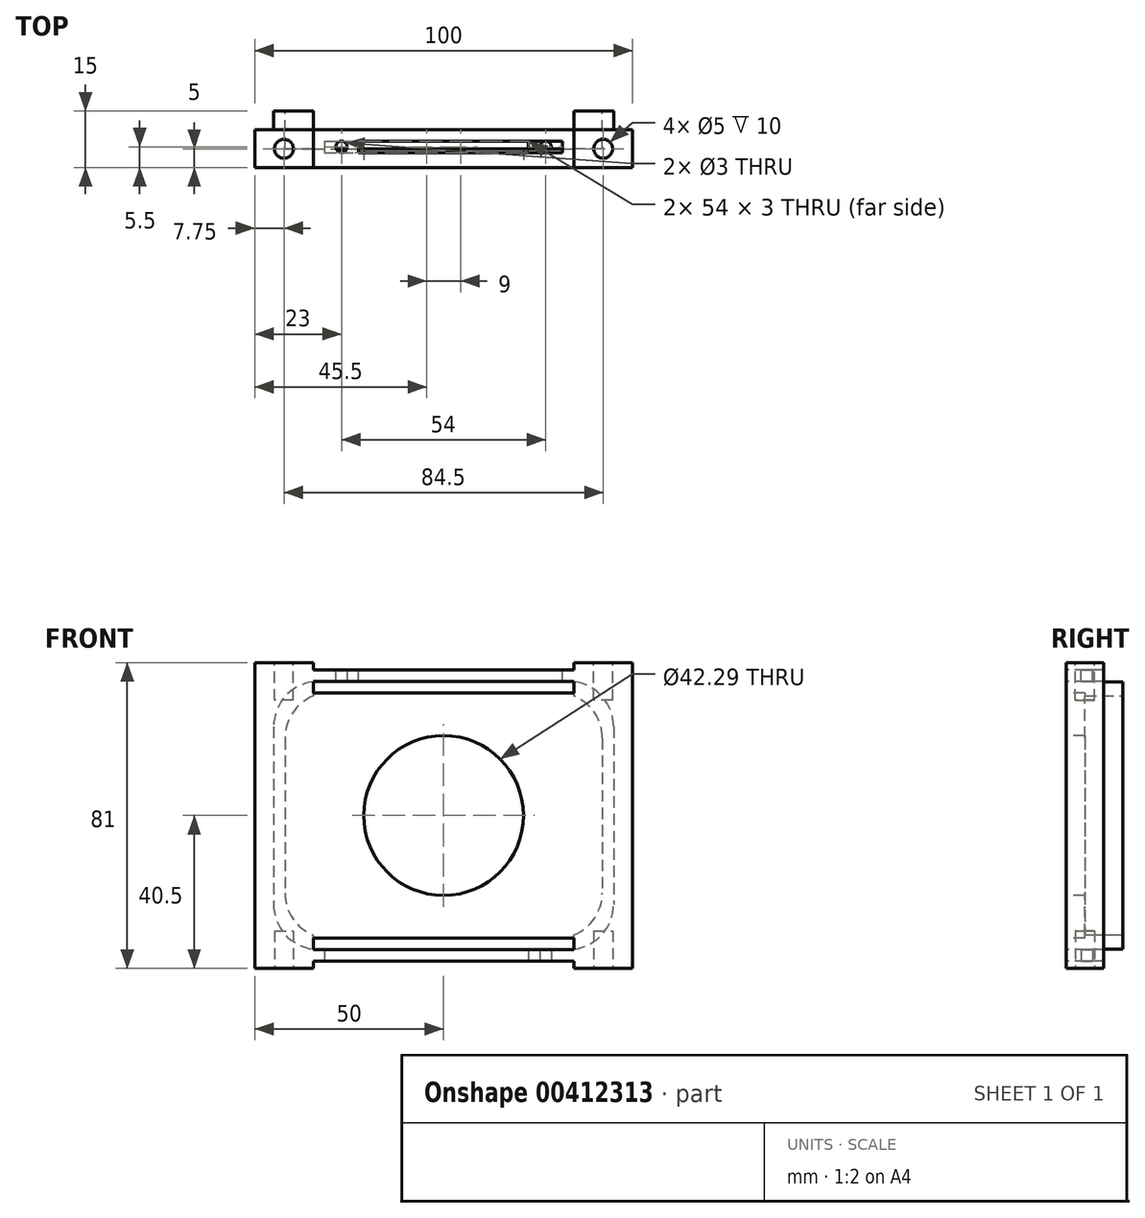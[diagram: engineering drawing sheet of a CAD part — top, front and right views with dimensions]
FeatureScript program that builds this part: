
annotation { "Feature Type Name" : "Feature", "Feature Type Description" : "" }
export const myFeature = defineFeature(function(context is Context, id is Id, definition is map)
    precondition{}
    {
        {
            var Q0;
            Q0=qCreatedBy(makeId("Front.planeOp"),FACE);
            var sketch = newSketch(context, id + "F0", { "sketchPlane" : qUnion([Q0])});
            skLineSegment(sketch, "E0.bottom", {"start": v(45, 35.5) * mm, "end": v(-45, 35.5) * mm});
            skLineSegment(sketch, "E0.top", {"start": v(45, -35.5) * mm, "end": v(-45, -35.5) * mm});
            skLineSegment(sketch, "E0.left", {"start": v(45, 35.5) * mm, "end": v(45, -35.5) * mm});
            skLineSegment(sketch, "E0.right", {"start": v(-45, 35.5) * mm, "end": v(-45, -35.5) * mm});
            skPoint(sketch, "E0.middle", {"position": v(0, 0) * mm});
            skSolve(sketch);
        }
        {
            var Q0;
            Q0 = qSketchRegion(id + "F0", true);
            extrude(context, id + "F1", {"entities" : qUnion([Q0]), "depth" : 5 * mm});
        }
        {
            var Q0;
            Q0=makeQuery(id+"F1.opExtrude","CAP_FACE",FACE,{"disambiguationData":[OSD([sQuery(id+"F0.wireOp",EDGE,"E0.bottom"),sQuery(id+"F0.wireOp",EDGE,"E0.top"),sQuery(id+"F0.wireOp",EDGE,"E0.left"),sQuery(id+"F0.wireOp",EDGE,"E0.right")])],"isStart":false});
            var sketch = newSketch(context, id + "F2", { "sketchPlane" : qUnion([Q0])});
            skLineSegment(sketch, "E1.bottom", {"start": v(50, 40.5) * mm, "end": v(-50, 40.5) * mm});
            skLineSegment(sketch, "E1.top", {"start": v(50, -40.5) * mm, "end": v(-50, -40.5) * mm});
            skLineSegment(sketch, "E1.left", {"start": v(50, 40.5) * mm, "end": v(50, -40.5) * mm});
            skLineSegment(sketch, "E1.right", {"start": v(-50, 40.5) * mm, "end": v(-50, -40.5) * mm});
            skPoint(sketch, "E1.middle", {"position": v(0, 0) * mm});
            skSolve(sketch);
        }
        {
            var Q0;
            Q0 = qSketchRegion(id + "F2", true);
            extrude(context, id + "F3", {"entities" : qUnion([Q0]), "operationType" : NewBodyOperationType.ADD, "depth" : 10 * mm});
        }
        {
            var Q0;
            Q0=makeQuery(id+"F3.opExtrude","CAP_FACE",FACE,{"disambiguationData":[OSD([sQuery(id+"F2.wireOp",EDGE,"E1.bottom"),sQuery(id+"F2.wireOp",EDGE,"E1.top"),sQuery(id+"F2.wireOp",EDGE,"E1.left"),sQuery(id+"F2.wireOp",EDGE,"E1.right")])],"isStart":false});
            var sketch = newSketch(context, id + "F4", { "sketchPlane" : qUnion([Q0])});
            skCircle(sketch, "E2", {"center": v(0, 0) * mm, "radius": 21.15 * mm});
            skSolve(sketch);
        }
        {
            var Q0;
            Q0 = qSketchRegion(id + "F4", true);
            extrude(context, id + "F5", {"entities" : qUnion([Q0]), "operationType" : NewBodyOperationType.REMOVE, "oppositeDirection" : true, "depth" : 25 * mm});
        }
        {
            var Q0;
            Q0=makeQuery(id+"F1.opExtrude","CAP_FACE",FACE,{"disambiguationData":[OSD([sQuery(id+"F0.wireOp",EDGE,"E0.bottom"),sQuery(id+"F0.wireOp",EDGE,"E0.top"),sQuery(id+"F0.wireOp",EDGE,"E0.left"),sQuery(id+"F0.wireOp",EDGE,"E0.right")])],"isStart":true});
            var sketch = newSketch(context, id + "F6", { "sketchPlane" : qUnion([Q0])});
            skLineSegment(sketch, "E3.bottom", {"start": v(42, 32.5) * mm, "end": v(-42, 32.5) * mm});
            skLineSegment(sketch, "E3.top", {"start": v(42, -32.5) * mm, "end": v(-42, -32.5) * mm});
            skLineSegment(sketch, "E3.left", {"start": v(42, 32.5) * mm, "end": v(42, -32.5) * mm});
            skLineSegment(sketch, "E3.right", {"start": v(-42, 32.5) * mm, "end": v(-42, -32.5) * mm});
            skPoint(sketch, "E3.middle", {"position": v(0, 0) * mm});
            skSolve(sketch);
        }
        {
            var Q0;
            Q0 = qSketchRegion(id + "F6", true);
            extrude(context, id + "F7", {"entities" : qUnion([Q0]), "operationType" : NewBodyOperationType.REMOVE, "oppositeDirection" : true, "depth" : 10 * mm});
        }
        {
            var Q0;
            Q0=makeQuery(id+"F7.boolean.opBoolean","COPY",EDGE,{"derivedFrom":makeQuery(id+"F7.opExtrude","SWEPT_EDGE",EDGE,{"disambiguationData":[OSD([sQuery(id+"F6.wireOp",EDGE,"E3.bottom"),sQuery(id+"F6.wireOp",EDGE,"E3.right")])]})});
            var Q1;
            Q1=makeQuery(id+"F7.boolean.opBoolean","COPY",EDGE,{"derivedFrom":makeQuery(id+"F7.opExtrude","SWEPT_EDGE",EDGE,{"disambiguationData":[OSD([sQuery(id+"F6.wireOp",EDGE,"E3.bottom"),sQuery(id+"F6.wireOp",EDGE,"E3.left")])]})});
            var Q2;
            Q2=makeQuery(id+"F7.boolean.opBoolean","COPY",EDGE,{"derivedFrom":makeQuery(id+"F7.opExtrude","SWEPT_EDGE",EDGE,{"disambiguationData":[OSD([sQuery(id+"F6.wireOp",EDGE,"E3.top"),sQuery(id+"F6.wireOp",EDGE,"E3.left")])]})});
            var Q3;
            Q3=makeQuery(id+"F7.boolean.opBoolean","COPY",EDGE,{"derivedFrom":makeQuery(id+"F7.opExtrude","SWEPT_EDGE",EDGE,{"disambiguationData":[OSD([sQuery(id+"F6.wireOp",EDGE,"E3.top"),sQuery(id+"F6.wireOp",EDGE,"E3.right")])]})});
            var Q4;
            Q4=makeQuery(id+"F1.opExtrude","SWEPT_EDGE",EDGE,{"disambiguationData":[OSD([sQuery(id+"F0.wireOp",EDGE,"E0.bottom"),sQuery(id+"F0.wireOp",EDGE,"E0.left")])]});
            var Q5;
            Q5=makeQuery(id+"F1.opExtrude","SWEPT_EDGE",EDGE,{"disambiguationData":[OSD([sQuery(id+"F0.wireOp",EDGE,"E0.top"),sQuery(id+"F0.wireOp",EDGE,"E0.left")])]});
            var Q6;
            Q6=makeQuery(id+"F1.opExtrude","SWEPT_EDGE",EDGE,{"disambiguationData":[OSD([sQuery(id+"F0.wireOp",EDGE,"E0.bottom"),sQuery(id+"F0.wireOp",EDGE,"E0.right")])]});
            var Q7;
            Q7=makeQuery(id+"F1.opExtrude","SWEPT_EDGE",EDGE,{"disambiguationData":[OSD([sQuery(id+"F0.wireOp",EDGE,"E0.top"),sQuery(id+"F0.wireOp",EDGE,"E0.right")])]});
            fillet(context, id + "F8", {"entities" : qUnion([Q0, Q1, Q2, Q3, Q4, Q5, Q6, Q7]), "radius" : 12 * mm, "tangentPropagation" : true, "allowEdgeOverflow" : false});
        }
        {
            var Q0;
            Q0=makeQuery(id+"F3.opExtrude","SWEPT_FACE",FACE,{"disambiguationData":[OSD([sQuery(id+"F2.wireOp",EDGE,"E1.bottom")])]});
            var sketch = newSketch(context, id + "F9", { "sketchPlane" : qUnion([Q0])});
            skLineSegment(sketch, "E4.bottom", {"start": v(34.5, -5) * mm, "end": v(-34.5, -5) * mm});
            skLineSegment(sketch, "E4.top", {"start": v(34.5, -15) * mm, "end": v(-34.5, -15) * mm});
            skLineSegment(sketch, "E4.left", {"start": v(34.5, -5) * mm, "end": v(34.5, -15) * mm});
            skLineSegment(sketch, "E4.right", {"start": v(-34.5, -5) * mm, "end": v(-34.5, -15) * mm});
            skPoint(sketch, "E4.middle", {"position": v(0, -10) * mm});
            skSolve(sketch);
        }
        {
            var Q0;
            Q0 = qSketchRegion(id + "F9", true);
            extrude(context, id + "F10", {"entities" : qUnion([Q0]), "operationType" : NewBodyOperationType.REMOVE, "oppositeDirection" : true, "depth" : 2 * mm});
        }
        {
            var Q0;
            Q0=makeQuery(id+"F3.opExtrude","SWEPT_FACE",FACE,{"disambiguationData":[OSD([sQuery(id+"F2.wireOp",EDGE,"E1.top")])]});
            var sketch = newSketch(context, id + "F11", { "sketchPlane" : qUnion([Q0])});
            skLineSegment(sketch, "E5.bottom", {"start": v(34.5, 5) * mm, "end": v(-34.5, 5) * mm});
            skLineSegment(sketch, "E5.top", {"start": v(34.5, 15) * mm, "end": v(-34.5, 15) * mm});
            skLineSegment(sketch, "E5.left", {"start": v(34.5, 5) * mm, "end": v(34.5, 15) * mm});
            skLineSegment(sketch, "E5.right", {"start": v(-34.5, 5) * mm, "end": v(-34.5, 15) * mm});
            skPoint(sketch, "E5.middle", {"position": v(0, 10) * mm});
            skSolve(sketch);
        }
        {
            var Q0;
            Q0 = qSketchRegion(id + "F11", true);
            extrude(context, id + "F12", {"entities" : qUnion([Q0]), "operationType" : NewBodyOperationType.REMOVE, "oppositeDirection" : true, "depth" : 2 * mm});
        }
        {
            var Q0;
            Q0=makeQuery(id+"F10.boolean.opBoolean","COPY",FACE,{"derivedFrom":makeQuery(id+"F10.opExtrude","CAP_FACE",FACE,{"disambiguationData":[OSD([sQuery(id+"F9.wireOp",EDGE,"E4.bottom"),sQuery(id+"F9.wireOp",EDGE,"E4.top"),sQuery(id+"F9.wireOp",EDGE,"E4.left"),sQuery(id+"F9.wireOp",EDGE,"E4.right")])],"isStart":false})});
            var sketch = newSketch(context, id + "F13", { "sketchPlane" : qUnion([Q0])});
            skLineSegment(sketch, "E6.bottom", {"start": v(31.5, -8) * mm, "end": v(-31.5, -8) * mm});
            skLineSegment(sketch, "E6.top", {"start": v(31.5, -11) * mm, "end": v(-31.5, -11) * mm});
            skLineSegment(sketch, "E6.left", {"start": v(31.5, -8) * mm, "end": v(31.5, -11) * mm});
            skLineSegment(sketch, "E6.right", {"start": v(-31.5, -8) * mm, "end": v(-31.5, -11) * mm});
            skPoint(sketch, "E6.middle", {"position": v(0, -9.5) * mm});
            skSolve(sketch);
        }
        {
            var Q0;
            Q0 = qSketchRegion(id + "F13", true);
            extrude(context, id + "F14", {"entities" : qUnion([Q0]), "operationType" : NewBodyOperationType.REMOVE, "oppositeDirection" : true, "depth" : 6 * mm});
        }
        {
            var Q0;
            Q0=makeQuery(id+"F3.opExtrude","CAP_FACE",FACE,{"disambiguationData":[OSD([sQuery(id+"F2.wireOp",EDGE,"E1.bottom"),sQuery(id+"F2.wireOp",EDGE,"E1.top"),sQuery(id+"F2.wireOp",EDGE,"E1.left"),sQuery(id+"F2.wireOp",EDGE,"E1.right")])],"isStart":false});
            var sketch = newSketch(context, id + "F15", { "sketchPlane" : qUnion([Q0])});
            skLineSegment(sketch, "E7.bottom", {"start": v(34.5, 32.5) * mm, "end": v(-34.5, 32.5) * mm});
            skLineSegment(sketch, "E7.top", {"start": v(34.5, 35.5) * mm, "end": v(-34.5, 35.5) * mm});
            skLineSegment(sketch, "E7.left", {"start": v(34.5, 32.5) * mm, "end": v(34.5, 35.5) * mm});
            skLineSegment(sketch, "E7.right", {"start": v(-34.5, 32.5) * mm, "end": v(-34.5, 35.5) * mm});
            skPoint(sketch, "E7.middle", {"position": v(0, 34) * mm});
            skSolve(sketch);
        }
        {
            var Q0;
            Q0 = qSketchRegion(id + "F15", true);
            extrude(context, id + "F16", {"entities" : qUnion([Q0]), "operationType" : NewBodyOperationType.REMOVE, "oppositeDirection" : true, "depth" : 25 * mm});
        }
        {
            var Q0;
            Q0=makeQuery(id+"F1.opExtrude","CAP_FACE",FACE,{"disambiguationData":[OSD([sQuery(id+"F0.wireOp",EDGE,"E0.bottom"),sQuery(id+"F0.wireOp",EDGE,"E0.top"),sQuery(id+"F0.wireOp",EDGE,"E0.left"),sQuery(id+"F0.wireOp",EDGE,"E0.right")])],"isStart":true});
            var sketch = newSketch(context, id + "F17", { "sketchPlane" : qUnion([Q0])});
            skLineSegment(sketch, "E8.bottom", {"start": v(-34.5, 35.4) * mm, "end": v(34.5, 35.4) * mm});
            skLineSegment(sketch, "E8.top", {"start": v(-34.5, 29.44) * mm, "end": v(34.5, 29.44) * mm});
            skLineSegment(sketch, "E8.left", {"start": v(-34.5, 35.4) * mm, "end": v(-34.5, 29.44) * mm});
            skLineSegment(sketch, "E8.right", {"start": v(34.5, 35.4) * mm, "end": v(34.5, 29.44) * mm});
            skSolve(sketch);
        }
        {
            var Q0;
            Q0 = qSketchRegion(id + "F17", true);
            extrude(context, id + "F18", {"entities" : qUnion([Q0]), "operationType" : NewBodyOperationType.REMOVE, "oppositeDirection" : true, "depth" : 10 * mm});
        }
        {
            var Q0;
            Q0=makeQuery(id+"F12.boolean.opBoolean","COPY",FACE,{"derivedFrom":makeQuery(id+"F12.opExtrude","CAP_FACE",FACE,{"disambiguationData":[OSD([sQuery(id+"F11.wireOp",EDGE,"E5.bottom"),sQuery(id+"F11.wireOp",EDGE,"E5.top"),sQuery(id+"F11.wireOp",EDGE,"E5.left"),sQuery(id+"F11.wireOp",EDGE,"E5.right")])],"isStart":false})});
            var sketch = newSketch(context, id + "F19", { "sketchPlane" : qUnion([Q0])});
            skLineSegment(sketch, "E9.bottom", {"start": v(-31.5, 8) * mm, "end": v(31.5, 8) * mm});
            skLineSegment(sketch, "E9.top", {"start": v(-31.5, 11) * mm, "end": v(31.5, 11) * mm});
            skLineSegment(sketch, "E9.left", {"start": v(-31.5, 8) * mm, "end": v(-31.5, 11) * mm});
            skLineSegment(sketch, "E9.right", {"start": v(31.5, 8) * mm, "end": v(31.5, 11) * mm});
            skPoint(sketch, "E9.middle", {"position": v(0, 9.5) * mm});
            skPoint(sketch, "E9.middle.positionSnap0", {"position": v(0, 5) * mm});
            skPoint(sketch, "E9.centerSnap0", {"position": v(0, 5) * mm});
            skSolve(sketch);
        }
        {
            var Q0;
            Q0 = qSketchRegion(id + "F19", true);
            extrude(context, id + "F20", {"entities" : qUnion([Q0]), "operationType" : NewBodyOperationType.REMOVE, "oppositeDirection" : true, "depth" : 6 * mm});
        }
        {
            var Q0;
            Q0=makeQuery(id+"F3.opExtrude","CAP_FACE",FACE,{"disambiguationData":[OSD([sQuery(id+"F2.wireOp",EDGE,"E1.bottom"),sQuery(id+"F2.wireOp",EDGE,"E1.top"),sQuery(id+"F2.wireOp",EDGE,"E1.left"),sQuery(id+"F2.wireOp",EDGE,"E1.right")])],"isStart":false});
            var sketch = newSketch(context, id + "F21", { "sketchPlane" : qUnion([Q0])});
            skLineSegment(sketch, "E10.bottom", {"start": v(34.5, -35.5) * mm, "end": v(-34.5, -35.5) * mm});
            skLineSegment(sketch, "E10.top", {"start": v(34.5, -32.5) * mm, "end": v(-34.5, -32.5) * mm});
            skLineSegment(sketch, "E10.left", {"start": v(34.5, -35.5) * mm, "end": v(34.5, -32.5) * mm});
            skLineSegment(sketch, "E10.right", {"start": v(-34.5, -35.5) * mm, "end": v(-34.5, -32.5) * mm});
            skPoint(sketch, "E10.middle", {"position": v(0, -34) * mm});
            skSolve(sketch);
        }
        {
            var Q0;
            Q0 = qSketchRegion(id + "F21", true);
            extrude(context, id + "F22", {"entities" : qUnion([Q0]), "operationType" : NewBodyOperationType.REMOVE, "oppositeDirection" : true, "depth" : 25 * mm});
        }
        {
            var Q0;
            {var subQ1=sQuery(id+"F0.wireOp",EDGE,"E0.left");var subQ2=sQuery(id+"F0.wireOp",EDGE,"E0.top");var subQ3=sQuery(id+"F0.wireOp",EDGE,"E0.bottom");Q0=makeQuery(id+"F22.boolean.opBoolean","SPLIT",FACE,{"disambiguationData":[TD([makeQuery(id+"F1.opExtrude","SWEPT_FACE",FACE,{"disambiguationData":[OSD([subQ1])]})])],"derivedFrom":makeQuery(id+"F1.opExtrude","CAP_FACE",FACE,{"disambiguationData":[OSD([subQ3,subQ2,subQ1,sQuery(id+"F0.wireOp",EDGE,"E0.right")])],"isStart":true})});}
            var sketch = newSketch(context, id + "F23", { "sketchPlane" : qUnion([Q0])});
            skLineSegment(sketch, "E11.bottom", {"start": v(-34.5, -35.4) * mm, "end": v(34.5, -35.4) * mm});
            skLineSegment(sketch, "E11.top", {"start": v(-34.5, -26.06) * mm, "end": v(34.5, -26.06) * mm});
            skLineSegment(sketch, "E11.left", {"start": v(-34.5, -35.4) * mm, "end": v(-34.5, -26.06) * mm});
            skLineSegment(sketch, "E11.right", {"start": v(34.5, -35.4) * mm, "end": v(34.5, -26.06) * mm});
            skSolve(sketch);
        }
        {
            var Q0;
            Q0 = qSketchRegion(id + "F23", true);
            extrude(context, id + "F24", {"entities" : qUnion([Q0]), "operationType" : NewBodyOperationType.REMOVE, "oppositeDirection" : true, "depth" : 10 * mm});
        }
        {
            var Q0;
            Q0=makeQuery(id+"F10.boolean.opBoolean","COPY",FACE,{"derivedFrom":makeQuery(id+"F10.opExtrude","CAP_FACE",FACE,{"disambiguationData":[OSD([sQuery(id+"F9.wireOp",EDGE,"E4.bottom"),sQuery(id+"F9.wireOp",EDGE,"E4.top"),sQuery(id+"F9.wireOp",EDGE,"E4.left"),sQuery(id+"F9.wireOp",EDGE,"E4.right")])],"isStart":false})});
            var sketch = newSketch(context, id + "F25", { "sketchPlane" : qUnion([Q0])});
            skLineSegment(sketch, "E12.bottom", {"start": v(-31.5, -8) * mm, "end": v(-22.5, -8) * mm});
            skLineSegment(sketch, "E12.top", {"start": v(-31.5, -11) * mm, "end": v(-22.5, -11) * mm});
            skLineSegment(sketch, "E12.left", {"start": v(-31.5, -8) * mm, "end": v(-31.5, -11) * mm});
            skLineSegment(sketch, "E12.right", {"start": v(-22.5, -8) * mm, "end": v(-22.5, -11) * mm});
            skSolve(sketch);
        }
        {
            var Q0;
            Q0 = qSketchRegion(id + "F25", true);
            extrude(context, id + "F26", {"entities" : qUnion([Q0]), "operationType" : NewBodyOperationType.ADD, "oppositeDirection" : true, "depth" : 3 * mm});
        }
        {
            var Q0;
            Q0=makeQuery(id+"F26.boolean.opBoolean","MERGE",FACE,{"derivedFrom":[makeQuery(id+"F10.boolean.opBoolean","COPY",FACE,{"derivedFrom":makeQuery(id+"F10.opExtrude","CAP_FACE",FACE,{"disambiguationData":[OSD([sQuery(id+"F9.wireOp",EDGE,"E4.bottom"),sQuery(id+"F9.wireOp",EDGE,"E4.top"),sQuery(id+"F9.wireOp",EDGE,"E4.left"),sQuery(id+"F9.wireOp",EDGE,"E4.right")])],"isStart":false})}),makeQuery(id+"F26.opExtrude","CAP_FACE",FACE,{"disambiguationData":[OSD([sQuery(id+"F25.wireOp",EDGE,"E12.bottom"),sQuery(id+"F25.wireOp",EDGE,"E12.top"),sQuery(id+"F25.wireOp",EDGE,"E12.left"),sQuery(id+"F25.wireOp",EDGE,"E12.right")])],"isStart":true})]});
            var sketch = newSketch(context, id + "F27", { "sketchPlane" : qUnion([Q0])});
            skCircle(sketch, "E13", {"center": v(-27, -9.5) * mm, "radius": 1.5 * mm});
            skSolve(sketch);
        }
        {
            var Q0;
            Q0 = qSketchRegion(id + "F27", true);
            extrude(context, id + "F28", {"entities" : qUnion([Q0]), "operationType" : NewBodyOperationType.REMOVE, "oppositeDirection" : true, "depth" : 3 * mm});
        }
        {
            var Q0;
            Q0=makeQuery(id+"F12.boolean.opBoolean","COPY",FACE,{"derivedFrom":makeQuery(id+"F12.opExtrude","CAP_FACE",FACE,{"disambiguationData":[OSD([sQuery(id+"F11.wireOp",EDGE,"E5.bottom"),sQuery(id+"F11.wireOp",EDGE,"E5.top"),sQuery(id+"F11.wireOp",EDGE,"E5.left"),sQuery(id+"F11.wireOp",EDGE,"E5.right")])],"isStart":false})});
            var sketch = newSketch(context, id + "F29", { "sketchPlane" : qUnion([Q0])});
            skLineSegment(sketch, "E14.bottom", {"start": v(31.5, 11) * mm, "end": v(22.5, 11) * mm});
            skLineSegment(sketch, "E14.top", {"start": v(31.5, 8) * mm, "end": v(22.5, 8) * mm});
            skLineSegment(sketch, "E14.left", {"start": v(31.5, 11) * mm, "end": v(31.5, 8) * mm});
            skLineSegment(sketch, "E14.right", {"start": v(22.5, 11) * mm, "end": v(22.5, 8) * mm});
            skSolve(sketch);
        }
        {
            var Q0;
            Q0 = qSketchRegion(id + "F29", true);
            extrude(context, id + "F30", {"entities" : qUnion([Q0]), "operationType" : NewBodyOperationType.ADD, "oppositeDirection" : true, "depth" : 3 * mm});
        }
        {
            var Q0;
            Q0=makeQuery(id+"F30.boolean.opBoolean","MERGE",FACE,{"derivedFrom":[makeQuery(id+"F12.boolean.opBoolean","COPY",FACE,{"derivedFrom":makeQuery(id+"F12.opExtrude","CAP_FACE",FACE,{"disambiguationData":[OSD([sQuery(id+"F11.wireOp",EDGE,"E5.bottom"),sQuery(id+"F11.wireOp",EDGE,"E5.top"),sQuery(id+"F11.wireOp",EDGE,"E5.left"),sQuery(id+"F11.wireOp",EDGE,"E5.right")])],"isStart":false})}),makeQuery(id+"F30.opExtrude","CAP_FACE",FACE,{"disambiguationData":[OSD([sQuery(id+"F29.wireOp",EDGE,"E14.bottom"),sQuery(id+"F29.wireOp",EDGE,"E14.top"),sQuery(id+"F29.wireOp",EDGE,"E14.left"),sQuery(id+"F29.wireOp",EDGE,"E14.right")])],"isStart":true})]});
            var sketch = newSketch(context, id + "F31", { "sketchPlane" : qUnion([Q0])});
            skCircle(sketch, "E15", {"center": v(27, 9.5) * mm, "radius": 1.5 * mm});
            skSolve(sketch);
        }
        {
            var Q0;
            Q0 = qSketchRegion(id + "F31", true);
            extrude(context, id + "F32", {"entities" : qUnion([Q0]), "operationType" : NewBodyOperationType.REMOVE, "oppositeDirection" : true, "depth" : 3 * mm});
        }
        {
            var Q0;
            {var subQ0=sQuery(id+"F2.wireOp",EDGE,"E1.right");var subQ3=sQuery(id+"F2.wireOp",EDGE,"E1.bottom");Q0=makeQuery(id+"F10.boolean.opBoolean","SPLIT",FACE,{"disambiguationData":[TD([makeQuery(id+"F3.opExtrude","SWEPT_FACE",FACE,{"disambiguationData":[OSD([subQ0])]})])],"derivedFrom":makeQuery(id+"F3.opExtrude","SWEPT_FACE",FACE,{"disambiguationData":[OSD([subQ3])]})});}
            var sketch = newSketch(context, id + "F33", { "sketchPlane" : qUnion([Q0])});
            skLineSegment(sketch, "E16", {"start": v(-34.5, -5) * mm, "end": v(-50, -15) * mm, "construction": true});
            skCircle(sketch, "E17", {"center": v(-42.25, -10) * mm, "radius": 2.5 * mm});
            skSolve(sketch);
        }
        {
            var Q0;
            Q0 = qSketchRegion(id + "F33", true);
            extrude(context, id + "F34", {"entities" : qUnion([Q0]), "operationType" : NewBodyOperationType.REMOVE, "oppositeDirection" : true, "depth" : 10 * mm});
        }
        {
            var Q0;
            {var subQ1=sQuery(id+"F2.wireOp",EDGE,"E1.left");var subQ3=sQuery(id+"F2.wireOp",EDGE,"E1.bottom");Q0=makeQuery(id+"F10.boolean.opBoolean","SPLIT",FACE,{"disambiguationData":[TD([makeQuery(id+"F3.opExtrude","SWEPT_FACE",FACE,{"disambiguationData":[OSD([subQ1])]})])],"derivedFrom":makeQuery(id+"F3.opExtrude","SWEPT_FACE",FACE,{"disambiguationData":[OSD([subQ3])]})});}
            var sketch = newSketch(context, id + "F35", { "sketchPlane" : qUnion([Q0])});
            skLineSegment(sketch, "E18", {"start": v(34.5, -5) * mm, "end": v(50, -15) * mm, "construction": true});
            skCircle(sketch, "E19", {"center": v(42.25, -10) * mm, "radius": 2.5 * mm});
            skSolve(sketch);
        }
        {
            var Q0;
            Q0 = qSketchRegion(id + "F35", true);
            extrude(context, id + "F36", {"entities" : qUnion([Q0]), "operationType" : NewBodyOperationType.REMOVE, "oppositeDirection" : true, "depth" : 10 * mm});
        }
        {
            var Q0;
            {var subQ0=sQuery(id+"F2.wireOp",EDGE,"E1.right");var subQ2=sQuery(id+"F2.wireOp",EDGE,"E1.top");Q0=makeQuery(id+"F12.boolean.opBoolean","SPLIT",FACE,{"disambiguationData":[TD([makeQuery(id+"F3.opExtrude","SWEPT_FACE",FACE,{"disambiguationData":[OSD([subQ0])]})])],"derivedFrom":makeQuery(id+"F3.opExtrude","SWEPT_FACE",FACE,{"disambiguationData":[OSD([subQ2])]})});}
            var sketch = newSketch(context, id + "F37", { "sketchPlane" : qUnion([Q0])});
            skLineSegment(sketch, "E20", {"start": v(-50, 15) * mm, "end": v(-34.5, 5) * mm, "construction": true});
            skCircle(sketch, "E21", {"center": v(-42.25, 10) * mm, "radius": 2.5 * mm});
            skSolve(sketch);
        }
        {
            var Q0;
            Q0 = qSketchRegion(id + "F37", true);
            extrude(context, id + "F38", {"entities" : qUnion([Q0]), "operationType" : NewBodyOperationType.REMOVE, "oppositeDirection" : true, "depth" : 10 * mm});
        }
        {
            var Q0;
            {var subQ1=sQuery(id+"F2.wireOp",EDGE,"E1.left");var subQ2=sQuery(id+"F2.wireOp",EDGE,"E1.top");Q0=makeQuery(id+"F12.boolean.opBoolean","SPLIT",FACE,{"disambiguationData":[TD([makeQuery(id+"F3.opExtrude","SWEPT_FACE",FACE,{"disambiguationData":[OSD([subQ1])]})])],"derivedFrom":makeQuery(id+"F3.opExtrude","SWEPT_FACE",FACE,{"disambiguationData":[OSD([subQ2])]})});}
            var sketch = newSketch(context, id + "F39", { "sketchPlane" : qUnion([Q0])});
            skLineSegment(sketch, "E22", {"start": v(50, 15) * mm, "end": v(34.5, 5) * mm, "construction": true});
            skCircle(sketch, "E23", {"center": v(42.25, 10) * mm, "radius": 2.5 * mm});
            skSolve(sketch);
        }
        {
            var Q0;
            Q0 = qSketchRegion(id + "F39", true);
            extrude(context, id + "F40", {"entities" : qUnion([Q0]), "operationType" : NewBodyOperationType.REMOVE, "oppositeDirection" : true, "depth" : 10 * mm});
        }
    });
